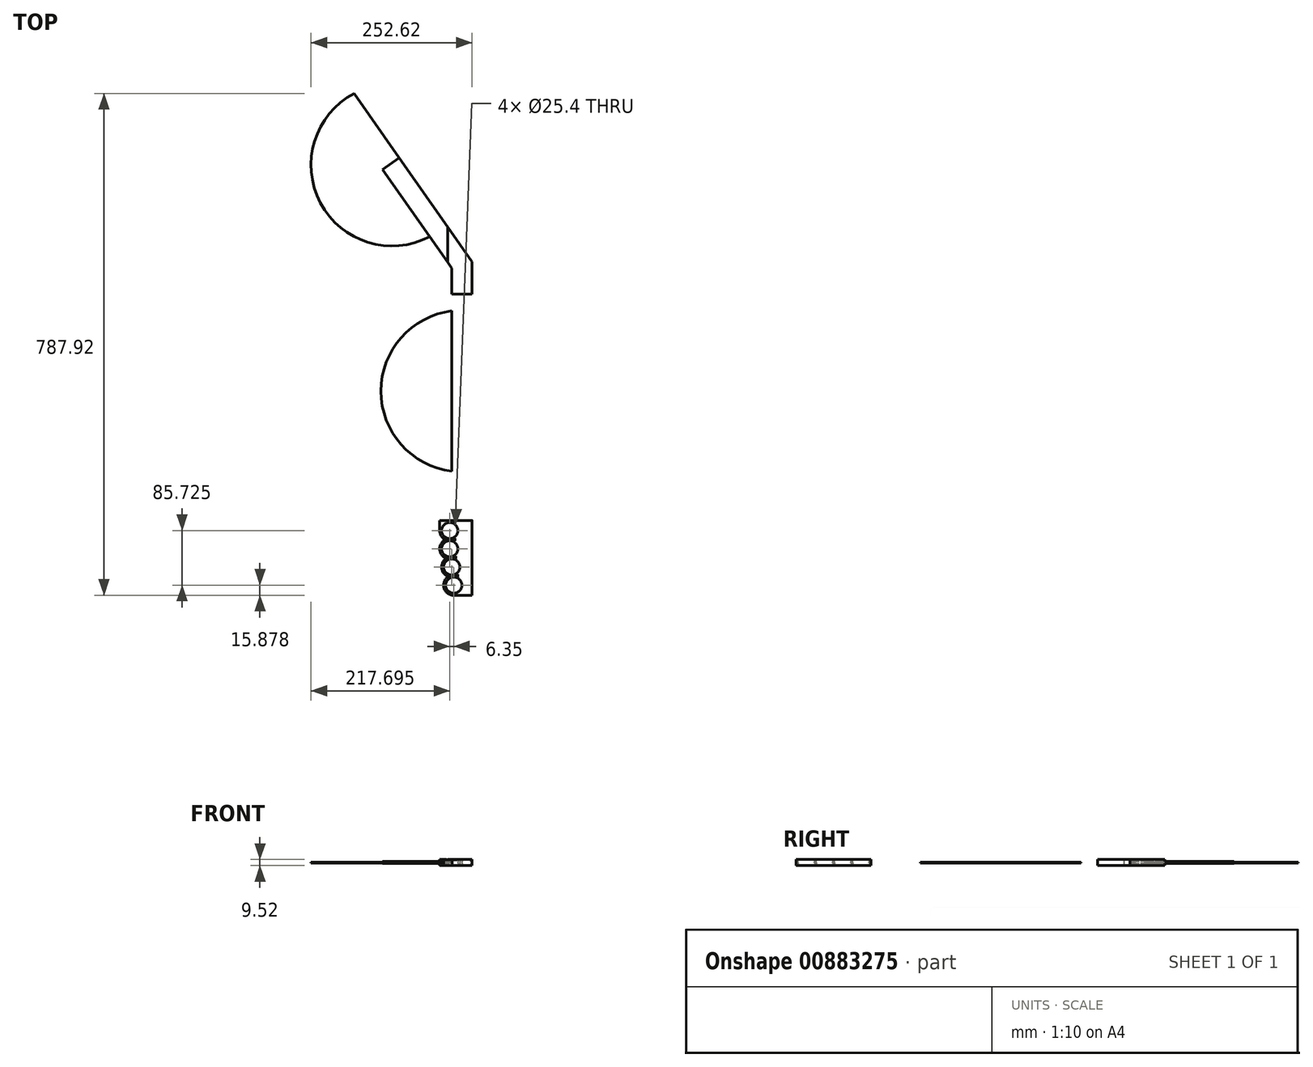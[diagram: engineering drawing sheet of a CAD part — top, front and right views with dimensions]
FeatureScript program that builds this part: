
annotation { "Feature Type Name" : "Feature", "Feature Type Description" : "" }
export const myFeature = defineFeature(function(context is Context, id is Id, definition is map)
    precondition{}
    {
        {
            var Q0;
            Q0=qCreatedBy(makeId("Top.planeOp"),FACE);
            var sketch = newSketch(context, id + "F0", { "sketchPlane" : qUnion([Q0])});
            skLineSegment(sketch, "E0.bottom", {"start": v(25.4, -58.74) * mm, "end": v(-25.4, -58.74) * mm});
            skLineSegment(sketch, "E0.top", {"start": v(25.4, 58.74) * mm, "end": v(-25.4, 58.74) * mm});
            skLineSegment(sketch, "E0.left", {"start": v(25.4, -58.74) * mm, "end": v(25.4, 58.74) * mm});
            skLineSegment(sketch, "E0.right", {"start": v(-25.4, -58.74) * mm, "end": v(-25.4, 58.74) * mm});
            skPoint(sketch, "E0.middle", {"position": v(0, 0) * mm});
            skCircle(sketch, "E1", {"center": v(-9.52, 42.86) * mm, "radius": 12.7 * mm});
            skCircle(sketch, "E2", {"center": v(-9.52, 14.29) * mm, "radius": 12.7 * mm});
            skCircle(sketch, "E3", {"center": v(-6.35, -14.29) * mm, "radius": 12.7 * mm});
            skCircle(sketch, "E4", {"center": v(-3.17, -42.86) * mm, "radius": 12.7 * mm});
            skArc(sketch, "E5", {"start": v(-11.86, -29.36) * mm, "mid": v(-18.87, -46.24) * mm, "end": v(-5.54, -58.74) * mm});
            skArc(sketch, "E6", {"start": v(-14.85, -0.67) * mm, "mid": v(-22.31, -15.95) * mm, "end": v(-11.86, -29.36) * mm});
            skArc(sketch, "E7", {"start": v(-16.44, 28.57) * mm, "mid": v(-25.38, 13.42) * mm, "end": v(-14.85, -0.67) * mm});
            skArc(sketch, "E8", {"start": v(-25.4, 42.86) * mm, "mid": v(-22.98, 34.43) * mm, "end": v(-16.44, 28.58) * mm});
            skLineSegment(sketch, "E9.bottom", {"start": v(-25.4, 58.74) * mm, "end": v(25.4, 58.74) * mm});
            skLineSegment(sketch, "E9.top", {"start": v(-6.35, 109.54) * mm, "end": v(25.4, 109.54) * mm});
            skLineSegment(sketch, "E9.right", {"start": v(25.4, 58.74) * mm, "end": v(25.4, 109.54) * mm});
            skLineSegment(sketch, "E10.bottom", {"start": v(25.4, 109.54) * mm, "end": v(-6.35, 109.54) * mm});
            skLineSegment(sketch, "E10.top", {"start": v(25.4, 414.34) * mm, "end": v(-6.35, 414.34) * mm});
            skLineSegment(sketch, "E10.left", {"start": v(25.4, 109.54) * mm, "end": v(25.4, 414.34) * mm});
            skLineSegment(sketch, "E10.right", {"start": v(-6.35, 109.54) * mm, "end": v(-6.35, 414.34) * mm});
            skLineSegment(sketch, "E11", {"start": v(-6.35, 109.54) * mm, "end": v(-25.4, 58.74) * mm});
            skPoint(sketch, "E12.start.orphan", {"position": v(-7.96, 59.6) * mm});
            skPoint(sketch, "E13.trimOffspring.end.orphan", {"position": v(-4.86, -60.78) * mm});
            skLineSegment(sketch, "E14", {"start": v(25.4, 414.34) * mm, "end": v(25.4, 465.14) * mm});
            skLineSegment(sketch, "E15", {"start": v(25.4, 465.14) * mm, "end": v(-12.7, 519.55) * mm});
            skLineSegment(sketch, "E16", {"start": v(-6.35, 414.34) * mm, "end": v(-6.35, 455.13) * mm});
            skLineSegment(sketch, "E17", {"start": v(-6.35, 455.13) * mm, "end": v(-12.7, 464.2) * mm});
            skLineSegment(sketch, "E18", {"start": v(-12.7, 519.55) * mm, "end": v(-12.7, 464.2) * mm});
            skLineSegment(sketch, "E19", {"start": v(-12.7, 519.55) * mm, "end": v(-88.67, 628.05) * mm});
            skLineSegment(sketch, "E20", {"start": v(-12.7, 464.2) * mm, "end": v(-114.68, 609.84) * mm});
            skLineSegment(sketch, "E21", {"start": v(-114.68, 609.84) * mm, "end": v(-88.67, 628.05) * mm});
            skPoint(sketch, "E22", {"position": v(9.53, 261.94) * mm});
            skPoint(sketch, "E22.positionSnap0", {"position": v(-6.35, 261.94) * mm});
            skPoint(sketch, "E22.positionSnap1", {"position": v(9.53, 414.34) * mm});
            skArc(sketch, "E23", {"start": v(9.53, 388.94) * mm, "mid": v(-117.47, 261.94) * mm, "end": v(9.53, 134.94) * mm});
            skPoint(sketch, "E24", {"position": v(-27.37, 512.83) * mm});
            skArc(sketch, "E25", {"start": v(-159.49, 729.18) * mm, "mid": v(-208.6, 550.68) * mm, "end": v(-27.37, 512.83) * mm});
            skLineSegment(sketch, "E26", {"start": v(-88.67, 628.05) * mm, "end": v(-162.8, 733.91) * mm});
            skSolve(sketch);
        }
        {
            var Q0;
            Q0=makeQuery(id+"F0.imprint","IMPRINT",FACE,{"disambiguationData":[TD([[makeQuery(id+"F0.imprint","IMPRINT",EDGE,{"derivedFrom":sQuery(id+"F0.wireOp",EDGE,"E10.top")}),-1.0]])]});
            var Q1;
            Q1=makeQuery(id+"F0.imprint","IMPRINT",FACE,{"disambiguationData":[TD([[makeQuery(id+"F0.imprint","IMPRINT",EDGE,{"derivedFrom":sQuery(id+"F0.wireOp",EDGE,"E9.bottom")}),1.0]])]});
            var Q2;
            {var subQ6=sQuery(id+"F0.wireOp",EDGE,"E0.left");Q2=makeQuery(id+"F0.imprint","IMPRINT",FACE,{"disambiguationData":[TD([[makeQuery(id+"F0.imprint","IMPRINT",EDGE,{"derivedFrom":subQ6}),1.0]])]});}
            extrude(context, id + "F1", {"entities" : qUnion([Q0, Q1, Q2]), "depth" : 4.76 * mm, "offsetDistance" : 25.4 * mm, "hasSecondDirection" : true, "secondDirectionOppositeDirection" : true, "secondDirectionDepth" : 4.76 * mm});
        }
        {
            var Q0;
            {var subQ1=sQuery(id+"F0.wireOp",EDGE,"E10.bottom");Q0=makeQuery(id+"F0.imprint","IMPRINT",FACE,{"disambiguationData":[TD([[makeQuery(id+"F0.imprint","IMPRINT",EDGE,{"derivedFrom":subQ1}),-1.0]])]});}
            var Q1;
            {var subQ3=sQuery(id+"F0.wireOp",EDGE,"E18");Q1=makeQuery(id+"F0.imprint","IMPRINT",FACE,{"disambiguationData":[TD([[makeQuery(id+"F0.imprint","IMPRINT",EDGE,{"derivedFrom":subQ3}),-1.0]])]});}
            extrude(context, id + "F2", {"entities" : qUnion([Q0, Q1]), "operationType" : NewBodyOperationType.ADD, "depth" : 1.59 * mm, "offsetDistance" : 25.4 * mm, "hasSecondDirection" : true, "secondDirectionOppositeDirection" : true, "secondDirectionDepth" : 1.59 * mm});
        }
        {
            var Q0;
            {var subQ0=sQuery(id+"F0.wireOp",EDGE,"E23");var subQ1=sQuery(id+"F0.wireOp",EDGE,"E10.right");var subQ2=makeQuery(id+"F0.imprint","INTERSECT",VERTEX,{"disambiguationData":[OD(0.0)],"derivedFrom":[subQ1,subQ0]});Q0=makeQuery(id+"F0.imprint","IMPRINT",FACE,{"disambiguationData":[TD([[makeQuery(id+"F0.imprint","IMPRINT",EDGE,{"disambiguationData":[TD([[subQ2,-1.0]])],"derivedFrom":subQ1}),1.0]])]});}
            var Q1;
            {var subQ0=sQuery(id+"F0.wireOp",EDGE,"E21");Q1=makeQuery(id+"F0.imprint","IMPRINT",FACE,{"disambiguationData":[TD([[makeQuery(id+"F0.imprint","IMPRINT",EDGE,{"derivedFrom":subQ0}),1.0]])]});}
            extrude(context, id + "F3", {"entities" : qUnion([Q0, Q1]), "operationType" : NewBodyOperationType.ADD, "depth" : 0.8 * mm, "offsetDistance" : 25.4 * mm, "hasSecondDirection" : true, "secondDirectionOppositeDirection" : true, "secondDirectionDepth" : 0.8 * mm});
        }
        {
            var Q0;
            Q0=makeQuery(id+"F1.opExtrude","CAP_EDGE",EDGE,{"disambiguationData":[OSD([sQuery(id+"F0.wireOp",EDGE,"E0.left"),sQuery(id+"F0.wireOp",EDGE,"E9.right")])],"isStart":false});
            var Q1;
            Q1=makeQuery(id+"F1.opExtrude","CAP_EDGE",EDGE,{"disambiguationData":[OSD([sQuery(id+"F0.wireOp",EDGE,"E0.left"),sQuery(id+"F0.wireOp",EDGE,"E9.right")])],"isStart":true});
            fillet(context, id + "F4", {"entities" : qUnion([Q0, Q1]), "radius" : 4.76 * mm, "tangentPropagation" : true, "allowEdgeOverflow" : false});
        }
        {
            var Q0;
            Q0=makeQuery(id+"F1.opExtrude","SWEPT_FACE",FACE,{"disambiguationData":[OSD([sQuery(id+"F0.wireOp",EDGE,"E1")])]});
            var Q1;
            Q1=makeQuery(id+"F1.opExtrude","SWEPT_FACE",FACE,{"disambiguationData":[OSD([sQuery(id+"F0.wireOp",EDGE,"E2")])]});
            var Q2;
            Q2=makeQuery(id+"F1.opExtrude","SWEPT_FACE",FACE,{"disambiguationData":[OSD([sQuery(id+"F0.wireOp",EDGE,"E3")])]});
            var Q3;
            Q3=makeQuery(id+"F1.opExtrude","SWEPT_FACE",FACE,{"disambiguationData":[OSD([sQuery(id+"F0.wireOp",EDGE,"E4")])]});
            fillet(context, id + "F5", {"entities" : qUnion([Q0, Q1, Q2, Q3]), "radius" : 4.76 * mm, "allowEdgeOverflow" : false});
        }
    });
